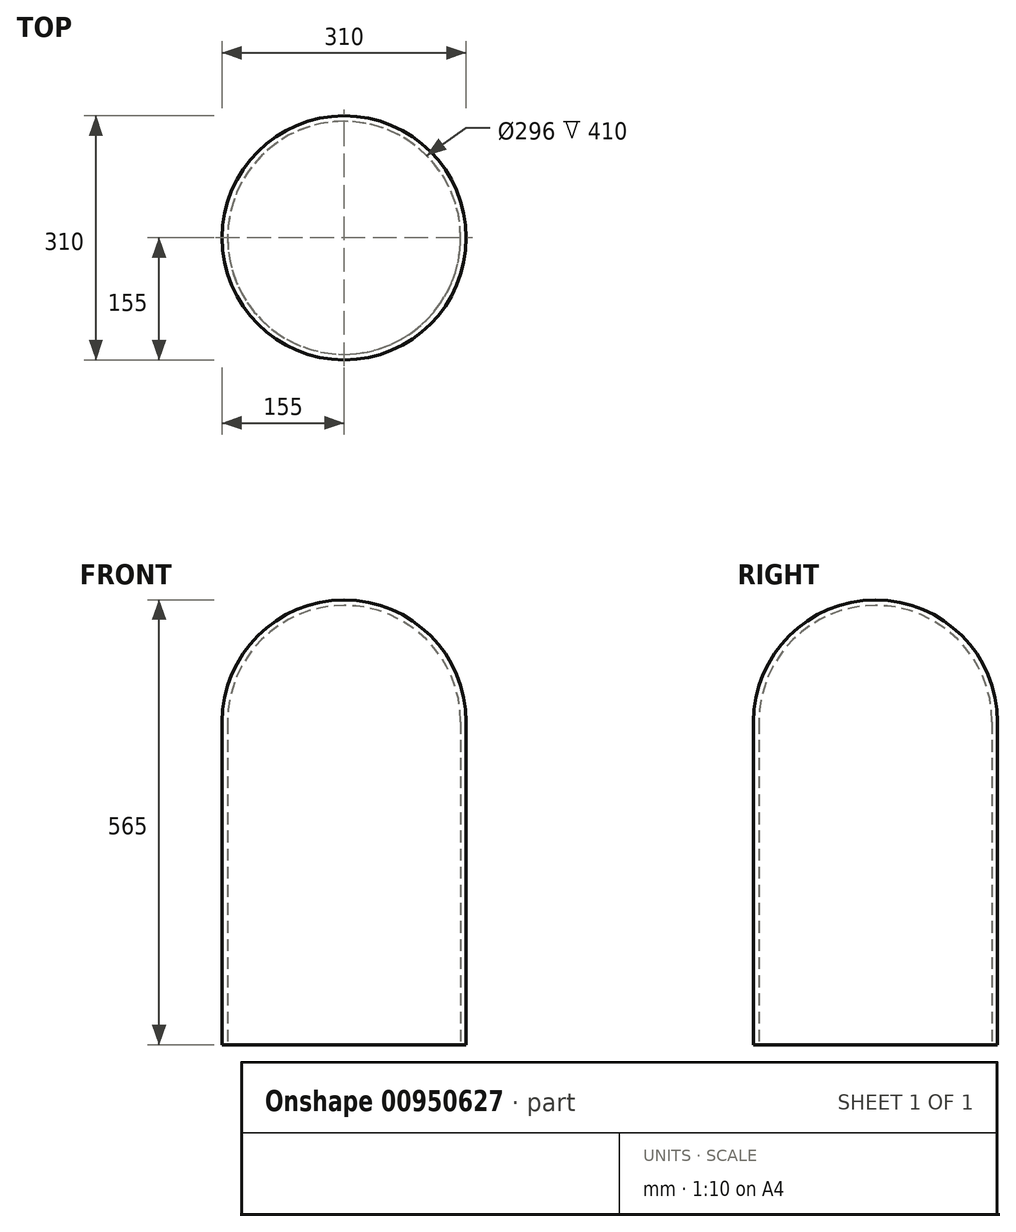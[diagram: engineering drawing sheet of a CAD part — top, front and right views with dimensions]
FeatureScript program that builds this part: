
annotation { "Feature Type Name" : "Feature", "Feature Type Description" : "" }
export const myFeature = defineFeature(function(context is Context, id is Id, definition is map)
    precondition{}
    {
        {
            var Q0;
            Q0=qCreatedBy(makeId("Top.planeOp"),FACE);
            var sketch = newSketch(context, id + "F0", { "sketchPlane" : qUnion([Q0])});
            skCircle(sketch, "E0", {"center": v(0, 0) * mm, "radius": 155 * mm});
            skSolve(sketch);
        }
        {
            var Q0;
            Q0=makeQuery(id+"F0.imprint","IMPRINT",FACE,{"disambiguationData":[TD([[makeQuery(id+"F0.imprint","IMPRINT",EDGE,{"derivedFrom":sQuery(id+"F0.wireOp",EDGE,"E0")}),1.0]])]});
            extrude(context, id + "F1", {"entities" : qUnion([Q0]), "depth" : 405 * mm, "offsetDistance" : 25 * mm});
        }
        {
            var Q0;
            Q0=makeQuery(id+"F1.opExtrude","CAP_FACE",FACE,{"disambiguationData":[OSD([sQuery(id+"F0.wireOp",EDGE,"E0")])],"isStart":false});
            var sketch = newSketch(context, id + "F2", { "sketchPlane" : qUnion([Q0])});
            skCircle(sketch, "E1.0", {"center": v(0, 0) * mm, "radius": 155 * mm});
            skLineSegment(sketch, "E2", {"start": v(0, 0) * mm, "end": v(0, -155) * mm});
            skLineSegment(sketch, "E3", {"start": v(0, -155) * mm, "end": v(0, 155) * mm});
            skArc(sketch, "E4", {"start": v(0, 148) * mm, "mid": v(-148, 0) * mm, "end": v(0, -148) * mm});
            skSolve(sketch);
        }
        {
            var Q0;
            {var subQ4=sQuery(id+"F2.wireOp",EDGE,"E4");Q0=makeQuery(id+"F2.imprint","IMPRINT",FACE,{"disambiguationData":[TD([[makeQuery(id+"F2.imprint","IMPRINT",EDGE,{"derivedFrom":subQ4}),-1.0]])]});}
            var Q1;
            Q1=sQuery(id+"F2.wireOp",EDGE,"E2");
            revolve(context, id + "F3", {"operationType" : NewBodyOperationType.ADD, "surfaceOperationType" : NewSurfaceOperationType.NEW, "entities" : qUnion([Q0]), "axis" : qUnion([Q1]), "revolveType" : RevolveType.FULL});
        }
        {
            var Q0;
            Q0=makeQuery(id+"F1.opExtrude","CAP_FACE",FACE,{"disambiguationData":[OSD([sQuery(id+"F0.wireOp",EDGE,"E0")])],"isStart":true});
            var sketch = newSketch(context, id + "F4", { "sketchPlane" : qUnion([Q0])});
            skCircle(sketch, "E5", {"center": v(0, 0) * mm, "radius": 148 * mm});
            skSolve(sketch);
        }
        {
            var Q0;
            Q0=qSketchRegion(id+"F4",true);
            extrude(context, id + "F5", {"entities" : qUnion([Q0]), "operationType" : NewBodyOperationType.REMOVE, "oppositeDirection" : true, "depth" : 405 * mm, "offsetDistance" : 25 * mm});
        }
        {
            var Q0;
            Q0=makeQuery(id+"F1.opExtrude","CAP_FACE",FACE,{"disambiguationData":[OSD([sQuery(id+"F0.wireOp",EDGE,"E0")])],"isStart":true});
            var sketch = newSketch(context, id + "F6", { "sketchPlane" : qUnion([Q0])});
            skCircle(sketch, "E6.0", {"center": v(0, 0) * mm, "radius": 155 * mm});
            skSolve(sketch);
        }
        {
            var Q0;
            Q0=makeQuery(id+"F6.imprint","IMPRINT",FACE,{"disambiguationData":[TD([[makeQuery(id+"F6.imprint","IMPRINT",EDGE,{"derivedFrom":sQuery(id+"F6.wireOp",EDGE,"E6.0")}),-1.0]])]});
            var Q1;
            Q1=makeQuery(id+"F6.imprint","IMPRINT",FACE,{"disambiguationData":[TD([[makeQuery(id+"F6.imprint","IMPRINT",EDGE,{"derivedFrom":makeQuery(id+"F5.boolean.opBoolean","COPY",EDGE,{"derivedFrom":makeQuery(id+"F5.opExtrude","CAP_EDGE",EDGE,{"disambiguationData":[OSD([sQuery(id+"F4.wireOp",EDGE,"E5")])],"isStart":true})})}),1.0]])]});
            extrude(context, id + "F7", {"entities" : qUnion([Q0, Q1]), "operationType" : NewBodyOperationType.ADD, "depth" : 5 * mm, "offsetDistance" : 25 * mm});
        }
    });
